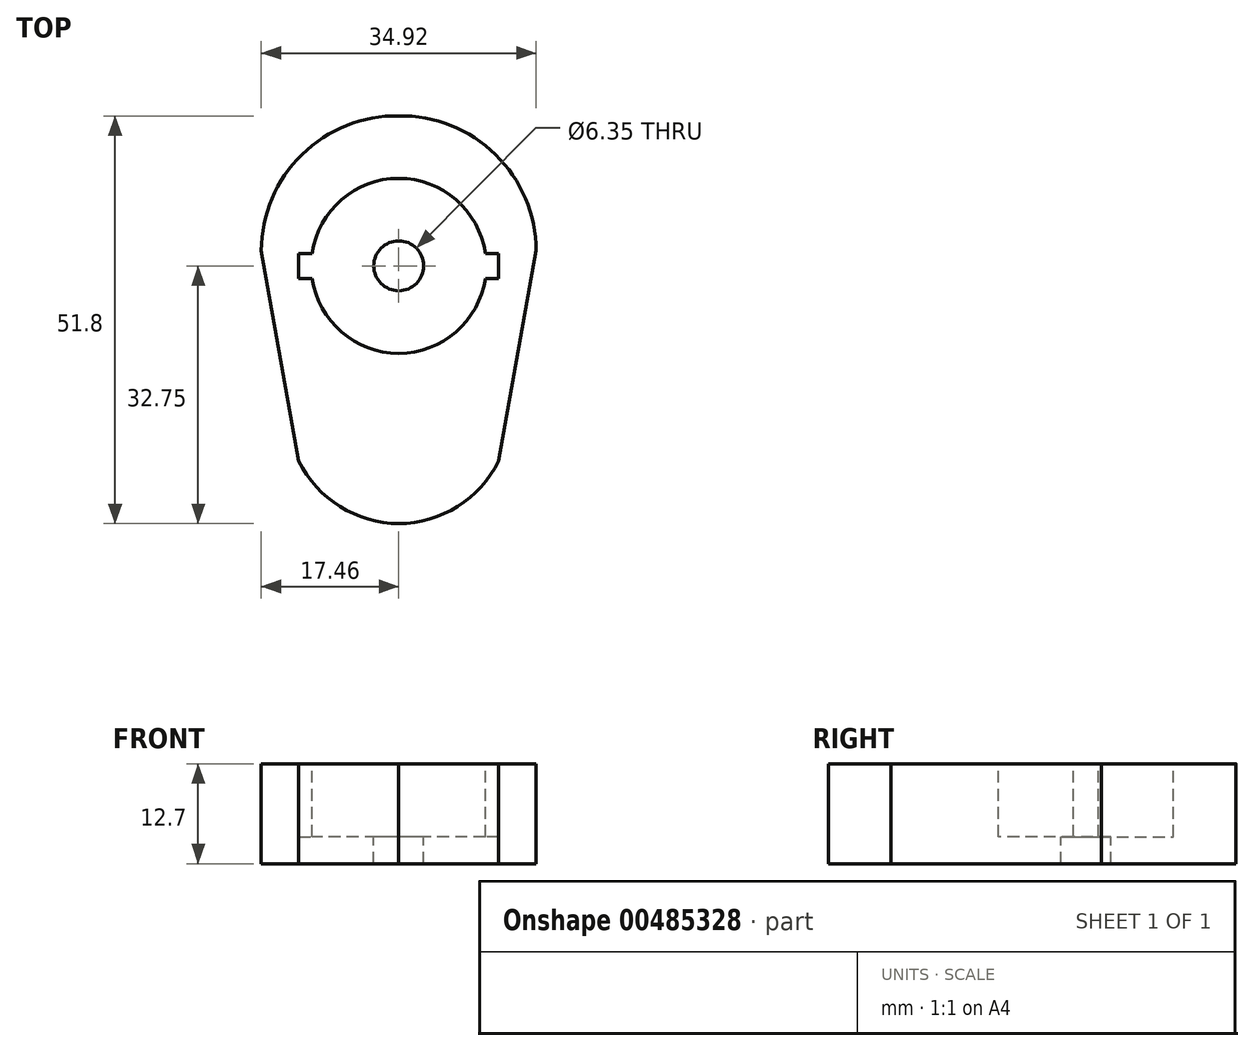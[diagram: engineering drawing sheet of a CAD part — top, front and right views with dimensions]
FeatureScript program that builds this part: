
annotation { "Feature Type Name" : "Feature", "Feature Type Description" : "" }
export const myFeature = defineFeature(function(context is Context, id is Id, definition is map)
    precondition{}
    {
        {
            var Q0;
            Q0=qCreatedBy(makeId("Top.planeOp"),FACE);
            var sketch = newSketch(context, id + "F0", { "sketchPlane" : qUnion([Q0])});
            skLineSegment(sketch, "E0", {"start": v(12.7, -24.81) * mm, "end": v(17.46, 1.93) * mm});
            skArc(sketch, "E1", {"start": v(0, -32.75) * mm, "mid": v(7.47, -30.57) * mm, "end": v(12.7, -24.81) * mm});
            skArc(sketch, "E2", {"start": v(17.46, 1.93) * mm, "mid": v(12.3, 14.12) * mm, "end": v(0, 19.05) * mm});
            skPoint(sketch, "E3.start.orphan", {"position": v(-12.7, -24.81) * mm});
            skPoint(sketch, "E4.start.orphan", {"position": v(0, -24.81) * mm});
            skArc(sketch, "E5.MirrorCS", {"start": v(-17.46, 1.93) * mm, "mid": v(-12.3, 14.12) * mm, "end": v(0, 19.05) * mm});
            skLineSegment(sketch, "E6.MirrorCS", {"start": v(-12.7, -24.81) * mm, "end": v(-17.46, 1.93) * mm});
            skArc(sketch, "E7.MirrorCS", {"start": v(0, -32.75) * mm, "mid": v(-7.47, -30.57) * mm, "end": v(-12.7, -24.81) * mm});
            skSolve(sketch);
        }
        {
            var Q0;
            Q0=makeQuery(id+"F0.imprint","IMPRINT",FACE,{"disambiguationData":[TD([[makeQuery(id+"F0.imprint","IMPRINT",EDGE,{"derivedFrom":sQuery(id+"F0.wireOp",EDGE,"E0")}),1.0]])]});
            extrude(context, id + "F1", {"entities" : qUnion([Q0]), "depth" : 12.7 * mm});
        }
        {
            var Q0;
            Q0=makeQuery(id+"F1.opExtrude","CAP_FACE",FACE,{"disambiguationData":[OSD([sQuery(id+"F0.wireOp",EDGE,"E0"),sQuery(id+"F0.wireOp",EDGE,"E1"),sQuery(id+"F0.wireOp",EDGE,"E2"),sQuery(id+"F0.wireOp",EDGE,"E5.MirrorCS"),sQuery(id+"F0.wireOp",EDGE,"E6.MirrorCS"),sQuery(id+"F0.wireOp",EDGE,"E7.MirrorCS")])],"isStart":false});
            var sketch = newSketch(context, id + "F2", { "sketchPlane" : qUnion([Q0])});
            skArc(sketch, "E8", {"start": v(11, 1.59) * mm, "mid": v(0, 11.11) * mm, "end": v(-11, 1.59) * mm});
            skLineSegment(sketch, "E9", {"start": v(-12.7, 0) * mm, "end": v(-12.7, 1.59) * mm});
            skLineSegment(sketch, "E10", {"start": v(-12.7, 1.59) * mm, "end": v(-11, 1.59) * mm});
            skLineSegment(sketch, "E11.MirrorCS", {"start": v(-12.7, 0) * mm, "end": v(-12.7, -1.59) * mm});
            skLineSegment(sketch, "E12.MirrorCS", {"start": v(-12.7, -1.59) * mm, "end": v(-11, -1.59) * mm});
            skLineSegment(sketch, "E13.MirrorCS", {"start": v(12.7, 0) * mm, "end": v(12.7, 1.59) * mm});
            skLineSegment(sketch, "E14.MirrorCS", {"start": v(12.7, 1.59) * mm, "end": v(11, 1.59) * mm});
            skLineSegment(sketch, "E15.MirrorCS", {"start": v(12.7, -1.59) * mm, "end": v(11, -1.59) * mm});
            skLineSegment(sketch, "E16.MirrorCS", {"start": v(12.7, 0) * mm, "end": v(12.7, -1.59) * mm});
            skPoint(sketch, "E17.start.orphan", {"position": v(-11.11, 0) * mm});
            skPoint(sketch, "E18.MirrorCS.end.orphan", {"position": v(12.7, 0.3) * mm});
            skPoint(sketch, "E18.MirrorCS.start.orphan", {"position": v(11.11, 0) * mm});
            skArc(sketch, "E19.trimOffspring", {"start": v(-11, -1.59) * mm, "mid": v(0, -11.11) * mm, "end": v(11, -1.59) * mm});
            skCircle(sketch, "E20", {"center": v(0, 0) * mm, "radius": 3.18 * mm});
            skSolve(sketch);
        }
        {
            var Q0;
            Q0=makeQuery(id+"F2.imprint","IMPRINT",FACE,{"disambiguationData":[TD([[makeQuery(id+"F2.imprint","IMPRINT",EDGE,{"derivedFrom":sQuery(id+"F2.wireOp",EDGE,"E8")}),1.0]])]});
            extrude(context, id + "F3", {"entities" : qUnion([Q0]), "operationType" : NewBodyOperationType.REMOVE, "oppositeDirection" : true, "depth" : 9.3 * mm});
        }
        {
            var Q0;
            Q0=makeQuery(id+"F3.boolean.opBoolean","SPLIT",FACE,{"disambiguationData":[TD([makeQuery(id+"F3.opExtrude","SWEPT_FACE",FACE,{"disambiguationData":[OSD([sQuery(id+"F2.wireOp",EDGE,"E20")])]})])],"derivedFrom":makeQuery(id+"F1.opExtrude","CAP_FACE",FACE,{"disambiguationData":[OSD([sQuery(id+"F0.wireOp",EDGE,"E0"),sQuery(id+"F0.wireOp",EDGE,"E1"),sQuery(id+"F0.wireOp",EDGE,"E2"),sQuery(id+"F0.wireOp",EDGE,"E5.MirrorCS"),sQuery(id+"F0.wireOp",EDGE,"E6.MirrorCS"),sQuery(id+"F0.wireOp",EDGE,"E7.MirrorCS")])],"isStart":false})});
            extrude(context, id + "F4", {"entities" : qUnion([Q0]), "operationType" : NewBodyOperationType.REMOVE, "oppositeDirection" : true, "depth" : 25.4 * mm});
        }
    });
